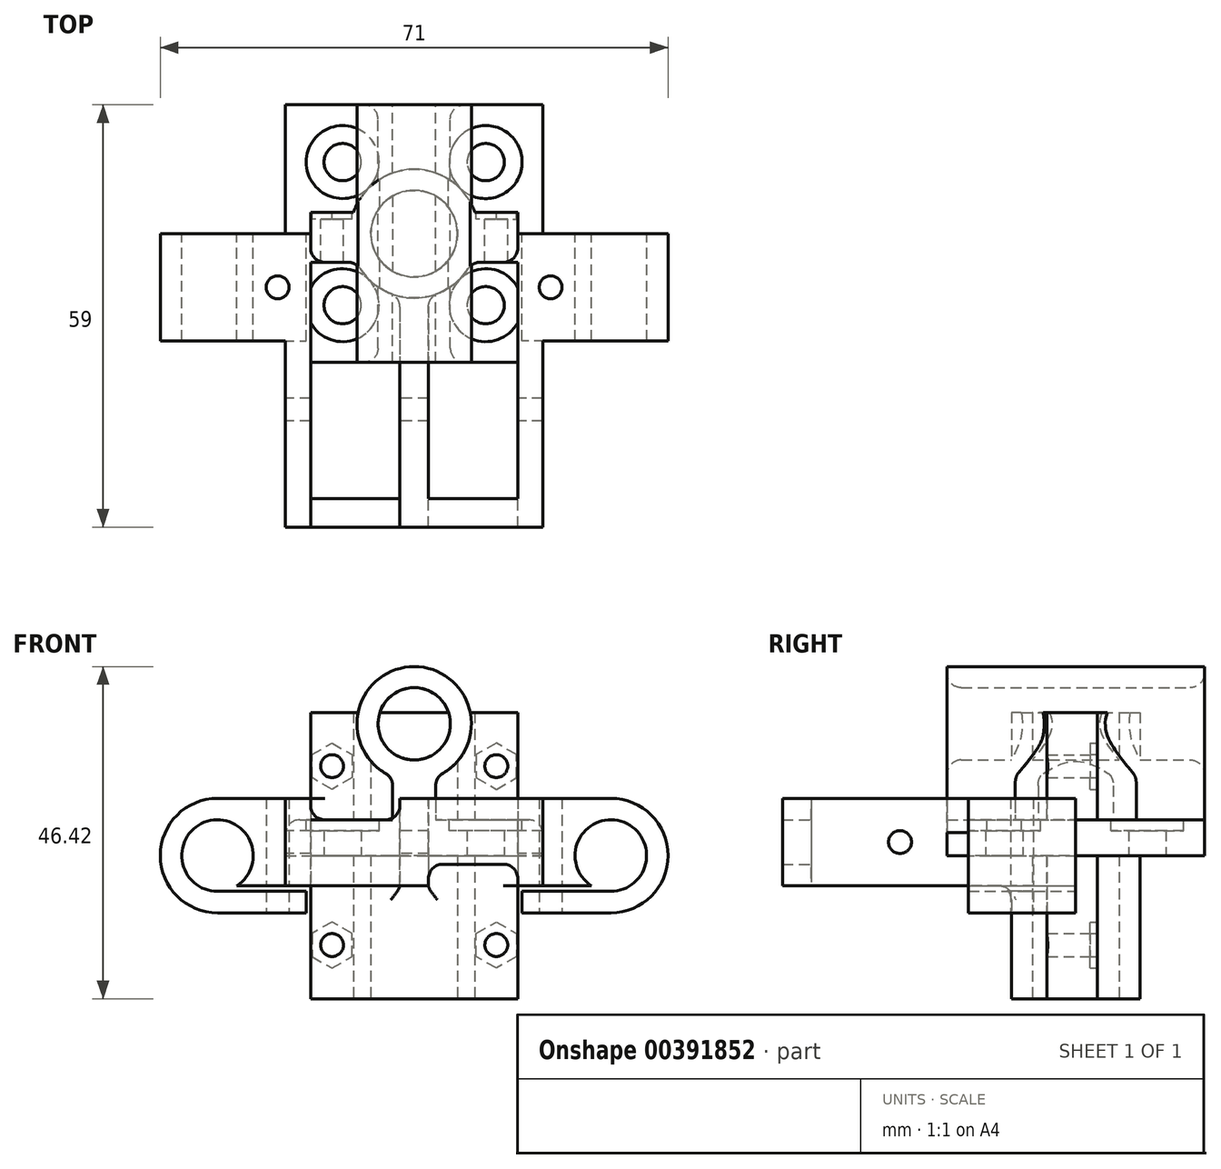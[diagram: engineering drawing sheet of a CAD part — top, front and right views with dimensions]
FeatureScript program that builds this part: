
annotation { "Feature Type Name" : "Feature", "Feature Type Description" : "" }
export const myFeature = defineFeature(function(context is Context, id is Id, definition is map)
    precondition{}
    {
        {
            var Q0;
            Q0=qCreatedBy(makeId("Top.planeOp"),FACE);
            var sketch = newSketch(context, id + "F0", { "sketchPlane" : qUnion([Q0])});
            skLineSegment(sketch, "E0.bottom", {"start": v(-18, 18) * mm, "end": v(18, 18) * mm});
            skLineSegment(sketch, "E0.top", {"start": v(-18, -18) * mm, "end": v(18, -18) * mm});
            skLineSegment(sketch, "E0.left", {"start": v(-18, 18) * mm, "end": v(-18, -18) * mm});
            skLineSegment(sketch, "E0.right", {"start": v(18, 18) * mm, "end": v(18, -18) * mm});
            skPoint(sketch, "E1", {"position": v(0, 18) * mm});
            skPoint(sketch, "E2", {"position": v(-18, 0) * mm});
            skCircle(sketch, "E3", {"center": v(-10, 10) * mm, "radius": 2.6 * mm});
            skCircle(sketch, "E4.MirrorC", {"center": v(-10, -10) * mm, "radius": 2.6 * mm});
            skCircle(sketch, "E5.MirrorC", {"center": v(10, 10) * mm, "radius": 2.6 * mm});
            skCircle(sketch, "E6.MirrorC", {"center": v(10, -10) * mm, "radius": 2.6 * mm});
            skSolve(sketch);
        }
        {
            var Q0;
            Q0=makeQuery(id+"F0.imprint","IMPRINT",FACE,{"disambiguationData":[TD([[makeQuery(id+"F0.imprint","IMPRINT",EDGE,{"derivedFrom":sQuery(id+"F0.wireOp",EDGE,"E0.bottom")}),-1.0]])]});
            extrude(context, id + "F1", {"entities" : qUnion([Q0]), "depth" : 5 * mm, "offsetDistance" : 25 * mm});
        }
        {
            var Q0;
            {var subQ0=sQuery(id+"F0.wireOp",EDGE,"E5.MirrorC");var subQ1=sQuery(id+"F0.wireOp",EDGE,"E0.top");var subQ7=sQuery(id+"F0.wireOp",EDGE,"E0.right");var subQ8=sQuery(id+"F0.wireOp",EDGE,"E0.bottom");var subQ9=sQuery(id+"F0.wireOp",EDGE,"E6.MirrorC");Q0=makeQuery(id+"F5.boolean.opBoolean","SPLIT",FACE,{"disambiguationData":[TD([makeQuery(id+"F1.opExtrude","SWEPT_FACE",FACE,{"disambiguationData":[OSD([subQ7])]})])],"derivedFrom":makeQuery(id+"F1.opExtrude","CAP_FACE",FACE,{"disambiguationData":[OSD([subQ8,subQ1,sQuery(id+"F0.wireOp",EDGE,"E0.left"),subQ7,sQuery(id+"F0.wireOp",EDGE,"E3"),sQuery(id+"F0.wireOp",EDGE,"E4.MirrorC"),subQ0,subQ9])],"isStart":false})});}
            var sketch = newSketch(context, id + "F2", { "sketchPlane" : qUnion([Q0])});
            skCircle(sketch, "E7", {"center": v(-10, 10) * mm, "radius": 5.1 * mm});
            skCircle(sketch, "E8.MirrorC", {"center": v(-10, -10) * mm, "radius": 5.1 * mm});
            skCircle(sketch, "E9.MirrorC", {"center": v(10, 10) * mm, "radius": 5.1 * mm});
            skCircle(sketch, "E10.MirrorC", {"center": v(10, -10) * mm, "radius": 5.1 * mm});
            skSolve(sketch);
        }
        {
            var Q0;
            Q0 = qSketchRegion(id + "F2", true);
            extrude(context, id + "F3", {"entities" : qUnion([Q0]), "operationType" : NewBodyOperationType.REMOVE, "oppositeDirection" : true, "depth" : 1.5 * mm, "offsetDistance" : 25 * mm});
        }
        {
            var Q0;
            Q0=qCreatedBy(makeId("Front.planeOp"),FACE);
            var sketch = newSketch(context, id + "F4", { "sketchPlane" : qUnion([Q0])});
            skLineSegment(sketch, "E11.top", {"start": v(-3, 5) * mm, "end": v(3, 5) * mm});
            skLineSegment(sketch, "E11.left", {"start": v(-3, 11) * mm, "end": v(-3, 5) * mm});
            skLineSegment(sketch, "E11.right", {"start": v(3, 11) * mm, "end": v(3, 5) * mm});
            skPoint(sketch, "E12", {"position": v(0, 11) * mm});
            skArc(sketch, "E13", {"start": v(3, 11) * mm, "mid": v(0, 26.42) * mm, "end": v(-3, 11) * mm});
            skCircle(sketch, "E14", {"center": v(0, 18.42) * mm, "radius": 5.05 * mm});
            skPoint(sketch, "E15", {"position": v(-3, 11) * mm});
            skSolve(sketch);
        }
        {
            var Q0;
            Q0=makeQuery(id+"F4.imprint","IMPRINT",FACE,{"disambiguationData":[TD([[makeQuery(id+"F4.imprint","IMPRINT",EDGE,{"derivedFrom":sQuery(id+"F4.wireOp",EDGE,"E11.top")}),1.0]])]});
            extrude(context, id + "F5", {"entities" : qUnion([Q0]), "operationType" : NewBodyOperationType.ADD, "depth" : 18 * mm, "offsetDistance" : 25 * mm, "hasSecondDirection" : true, "secondDirectionOppositeDirection" : true, "secondDirectionDepth" : 18 * mm});
        }
        {
            var Q0;
            Q0=makeQuery(id+"F5.opExtrude","CAP_EDGE",EDGE,{"disambiguationData":[OSD([sQuery(id+"F4.wireOp",EDGE,"E14")])],"isStart":false});
            var Q1;
            Q1=makeQuery(id+"F5.opExtrude","SWEPT_EDGE",EDGE,{"disambiguationData":[OSD([sQuery(id+"F4.wireOp",EDGE,"E11.top"),sQuery(id+"F4.wireOp",EDGE,"E11.left")])]});
            var Q2;
            Q2=makeQuery(id+"F5.opExtrude","SWEPT_EDGE",EDGE,{"disambiguationData":[OSD([sQuery(id+"F4.wireOp",EDGE,"E11.top"),sQuery(id+"F4.wireOp",EDGE,"E11.right")])]});
            var Q3;
            Q3=makeQuery(id+"F5.opExtrude","SWEPT_EDGE",EDGE,{"disambiguationData":[OSD([sQuery(id+"F4.wireOp",EDGE,"E11.right"),sQuery(id+"F4.wireOp",EDGE,"E13")])]});
            var Q4;
            Q4=makeQuery(id+"F5.opExtrude","SWEPT_EDGE",EDGE,{"disambiguationData":[OSD([sQuery(id+"F4.wireOp",EDGE,"E11.left"),sQuery(id+"F4.wireOp",EDGE,"E13")])]});
            var Q5;
            Q5=makeQuery(id+"F5.opExtrude","CAP_EDGE",EDGE,{"disambiguationData":[OSD([sQuery(id+"F4.wireOp",EDGE,"E14")])],"isStart":true});
            var Q6;
            Q6=makeQuery(id+"F1.opExtrude","CAP_EDGE",EDGE,{"disambiguationData":[OSD([sQuery(id+"F0.wireOp",EDGE,"E0.left")])],"isStart":false});
            var Q7;
            Q7=makeQuery(id+"F1.opExtrude","CAP_EDGE",EDGE,{"disambiguationData":[OSD([sQuery(id+"F0.wireOp",EDGE,"E0.right")])],"isStart":false});
            fillet(context, id + "F6", {"entities" : qUnion([Q0, Q1, Q2, Q3, Q4, Q5, Q6, Q7]), "radius" : 2 * mm, "tangentPropagation" : true, "allowEdgeOverflow" : false});
        }
        {
            var Q0;
            Q0=qCreatedBy(makeId("Top.planeOp"),FACE);
            var sketch = newSketch(context, id + "F7", { "sketchPlane" : qUnion([Q0])});
            skArc(sketch, "E16", {"start": v(6.05, 0) * mm, "mid": v(0, 6.05) * mm, "end": v(-6.05, 0) * mm});
            skArc(sketch, "E17", {"start": v(8.49, 3) * mm, "mid": v(0, 9) * mm, "end": v(-8.49, 3) * mm});
            skLineSegment(sketch, "E18", {"start": v(-9, 0) * mm, "end": v(-14.49, 0) * mm});
            skLineSegment(sketch, "E19", {"start": v(-14.49, 0) * mm, "end": v(-14.49, 3) * mm});
            skLineSegment(sketch, "E20", {"start": v(-14.49, 3) * mm, "end": v(-8.49, 3) * mm});
            skLineSegment(sketch, "E21", {"start": v(-6.05, 0) * mm, "end": v(-9, 0) * mm});
            skLineSegment(sketch, "E22.MirrorCS", {"start": v(14.49, 3) * mm, "end": v(8.49, 3) * mm});
            skLineSegment(sketch, "E23.MirrorCS", {"start": v(14.49, 0) * mm, "end": v(14.49, 3) * mm});
            skLineSegment(sketch, "E24.MirrorCS", {"start": v(9, 0) * mm, "end": v(14.49, 0) * mm});
            skLineSegment(sketch, "E25.MirrorCS", {"start": v(6.05, 0) * mm, "end": v(9, 0) * mm});
            skPoint(sketch, "E26.orphan", {"position": v(9, 0) * mm});
            skSolve(sketch);
        }
        {
            var Q0;
            Q0=makeQuery(id+"F7.imprint","IMPRINT",FACE,{"disambiguationData":[TD([[makeQuery(id+"F7.imprint","IMPRINT",EDGE,{"derivedFrom":sQuery(id+"F7.wireOp",EDGE,"E16")}),-1.0]])]});
            extrude(context, id + "F8", {"entities" : qUnion([Q0]), "depth" : 20 * mm, "offsetDistance" : 25 * mm, "hasSecondDirection" : true, "secondDirectionOppositeDirection" : true, "secondDirectionDepth" : 20 * mm});
        }
        {
            var Q0;
            Q0=makeQuery(id+"F8.opExtrude","SWEPT_FACE",FACE,{"disambiguationData":[OSD([sQuery(id+"F7.wireOp",EDGE,"E20")])]});
            var sketch = newSketch(context, id + "F9", { "sketchPlane" : qUnion([Q0])});
            skCircle(sketch, "E27", {"center": v(11.49, -12.5) * mm, "radius": 1.6 * mm});
            skCircle(sketch, "E28.MirrorC", {"center": v(11.49, 12.5) * mm, "radius": 1.6 * mm});
            skCircle(sketch, "E29.MirrorC", {"center": v(-11.49, -12.5) * mm, "radius": 1.6 * mm});
            skCircle(sketch, "E30.MirrorC", {"center": v(-11.49, 12.5) * mm, "radius": 1.6 * mm});
            skSolve(sketch);
        }
        {
            var Q0;
            Q0=makeQuery(id+"F8.opExtrude","SWEPT_FACE",FACE,{"disambiguationData":[OSD([sQuery(id+"F7.wireOp",EDGE,"E20")])]});
            var sketch = newSketch(context, id + "F10", { "sketchPlane" : qUnion([Q0])});
            skCircle(sketch, "E31.cCircle", {"center": v(11.49, -12.5) * mm, "radius": 2.8 * mm, "construction": true});
            skLineSegment(sketch, "E31.0", {"start": v(8.69, -10.88) * mm, "end": v(11.49, -9.27) * mm});
            skLineSegment(sketch, "E31.1", {"start": v(11.49, -9.27) * mm, "end": v(14.29, -10.88) * mm});
            skLineSegment(sketch, "E31.2", {"start": v(14.29, -10.88) * mm, "end": v(14.29, -14.12) * mm});
            skLineSegment(sketch, "E31.3", {"start": v(14.29, -14.12) * mm, "end": v(11.49, -15.73) * mm});
            skLineSegment(sketch, "E31.4", {"start": v(11.49, -15.73) * mm, "end": v(8.69, -14.12) * mm});
            skLineSegment(sketch, "E31.5", {"start": v(8.69, -14.12) * mm, "end": v(8.69, -10.88) * mm});
            skPoint(sketch, "E31.0.midPoint", {"position": v(10.09, -10.08) * mm});
            skPoint(sketch, "E32.MirrorP", {"position": v(10.09, 10.08) * mm});
            skCircle(sketch, "E33.MirrorC", {"center": v(11.49, 12.5) * mm, "radius": 2.8 * mm, "construction": true});
            skLineSegment(sketch, "E34.MirrorCS", {"start": v(8.69, 10.88) * mm, "end": v(11.49, 9.27) * mm});
            skLineSegment(sketch, "E35.MirrorCS", {"start": v(11.49, 9.27) * mm, "end": v(14.29, 10.88) * mm});
            skLineSegment(sketch, "E36.MirrorCS", {"start": v(14.29, 10.88) * mm, "end": v(14.29, 14.12) * mm});
            skLineSegment(sketch, "E37.MirrorCS", {"start": v(14.29, 14.12) * mm, "end": v(11.49, 15.73) * mm});
            skLineSegment(sketch, "E38.MirrorCS", {"start": v(11.49, 15.73) * mm, "end": v(8.69, 14.12) * mm});
            skLineSegment(sketch, "E39.MirrorCS", {"start": v(8.69, 14.12) * mm, "end": v(8.69, 10.88) * mm});
            skLineSegment(sketch, "E40.MirrorCS", {"start": v(-11.49, 9.27) * mm, "end": v(-14.29, 10.88) * mm});
            skLineSegment(sketch, "E41.MirrorCS", {"start": v(-8.69, 10.88) * mm, "end": v(-11.49, 9.27) * mm});
            skCircle(sketch, "E42.MirrorC", {"center": v(-11.49, 12.5) * mm, "radius": 2.8 * mm, "construction": true});
            skLineSegment(sketch, "E43.MirrorCS", {"start": v(-8.69, -14.12) * mm, "end": v(-8.69, -10.88) * mm});
            skLineSegment(sketch, "E44.MirrorCS", {"start": v(-11.49, -15.73) * mm, "end": v(-8.69, -14.12) * mm});
            skLineSegment(sketch, "E45.MirrorCS", {"start": v(-14.29, -14.12) * mm, "end": v(-11.49, -15.73) * mm});
            skLineSegment(sketch, "E46.MirrorCS", {"start": v(-14.29, -10.88) * mm, "end": v(-14.29, -14.12) * mm});
            skLineSegment(sketch, "E47.MirrorCS", {"start": v(-11.49, -9.27) * mm, "end": v(-14.29, -10.88) * mm});
            skLineSegment(sketch, "E48.MirrorCS", {"start": v(-8.69, -10.88) * mm, "end": v(-11.49, -9.27) * mm});
            skCircle(sketch, "E49.MirrorC", {"center": v(-11.49, -12.5) * mm, "radius": 2.8 * mm, "construction": true});
            skLineSegment(sketch, "E50.MirrorCS", {"start": v(-8.69, 14.12) * mm, "end": v(-8.69, 10.88) * mm});
            skPoint(sketch, "E51.MirrorP", {"position": v(-10.09, 10.08) * mm});
            skLineSegment(sketch, "E52.MirrorCS", {"start": v(-11.49, 15.73) * mm, "end": v(-8.69, 14.12) * mm});
            skPoint(sketch, "E53.MirrorP", {"position": v(-10.09, -10.08) * mm});
            skLineSegment(sketch, "E54.MirrorCS", {"start": v(-14.29, 14.12) * mm, "end": v(-11.49, 15.73) * mm});
            skLineSegment(sketch, "E55.MirrorCS", {"start": v(-14.29, 10.88) * mm, "end": v(-14.29, 14.12) * mm});
            skSolve(sketch);
        }
        {
            var Q0;
            Q0 = qSketchRegion(id + "F10", true);
            extrude(context, id + "F11", {"entities" : qUnion([Q0]), "operationType" : NewBodyOperationType.REMOVE, "oppositeDirection" : true, "depth" : 1 * mm, "offsetDistance" : 25 * mm});
        }
        {
            var Q0;
            Q0=qCreatedBy(makeId("Top.planeOp"),FACE);
            var sketch = newSketch(context, id + "F12", { "sketchPlane" : qUnion([Q0])});
            skPoint(sketch, "E56.0", {"position": v(6.05, 0) * mm});
            skPoint(sketch, "E57.0", {"position": v(-6.05, 0) * mm});
            skArc(sketch, "E58", {"start": v(-6.05, 0) * mm, "mid": v(0, -6.05) * mm, "end": v(6.05, 0) * mm});
            skLineSegment(sketch, "E59", {"start": v(6.05, 0) * mm, "end": v(14.49, 0) * mm});
            skLineSegment(sketch, "E60", {"start": v(14.49, 0) * mm, "end": v(14.49, -4) * mm});
            skLineSegment(sketch, "E61", {"start": v(14.49, -4) * mm, "end": v(8.06, -4) * mm});
            skLineSegment(sketch, "E62.MirrorCS", {"start": v(-6.05, 0) * mm, "end": v(-14.49, 0) * mm});
            skLineSegment(sketch, "E63.MirrorCS", {"start": v(-14.49, 0) * mm, "end": v(-14.49, -4) * mm});
            skLineSegment(sketch, "E64.MirrorCS", {"start": v(-14.49, -4) * mm, "end": v(-8.06, -4) * mm});
            skArc(sketch, "E65", {"start": v(-8.06, -4) * mm, "mid": v(0, -9) * mm, "end": v(8.06, -4) * mm});
            skPoint(sketch, "E66.orphan", {"position": v(4.54, -4) * mm});
            skPoint(sketch, "E67.orphan", {"position": v(-4.54, -4) * mm});
            skSolve(sketch);
        }
        {
            var Q0;
            Q0=makeQuery(id+"F12.imprint","IMPRINT",FACE,{"disambiguationData":[TD([[makeQuery(id+"F12.imprint","IMPRINT",EDGE,{"derivedFrom":sQuery(id+"F12.wireOp",EDGE,"E58")}),-1.0]])]});
            extrude(context, id + "F13", {"entities" : qUnion([Q0]), "depth" : 20 * mm, "offsetDistance" : 25 * mm, "hasSecondDirection" : true, "secondDirectionOppositeDirection" : true, "secondDirectionDepth" : 20 * mm});
        }
        {
            var Q0;
            Q0 = qSketchRegion(id + "F9", true);
            extrude(context, id + "F14", {"entities" : qUnion([Q0]), "operationType" : NewBodyOperationType.REMOVE, "oppositeDirection" : true, "depth" : 10 * mm, "offsetDistance" : 25 * mm});
        }
        {
            var Q0;
            Q0=qCreatedBy(makeId("Front.planeOp"),FACE);
            var sketch = newSketch(context, id + "F15", { "sketchPlane" : qUnion([Q0])});
            skArc(sketch, "E68", {"start": v(27.5, -5) * mm, "mid": v(28.91, 4.8) * mm, "end": v(24.79, -4.2) * mm});
            skLineSegment(sketch, "E69", {"start": v(27.5, 8) * mm, "end": v(14.49, 8) * mm});
            skLineSegment(sketch, "E70", {"start": v(14.49, 8) * mm, "end": v(14.49, -4.2) * mm});
            skLineSegment(sketch, "E71", {"start": v(14.49, -4.2) * mm, "end": v(24.79, -4.2) * mm});
            skLineSegment(sketch, "E72", {"start": v(27.5, -5) * mm, "end": v(15.09, -5) * mm});
            skLineSegment(sketch, "E73", {"start": v(15.09, -5) * mm, "end": v(15.09, -8) * mm});
            skLineSegment(sketch, "E74", {"start": v(15.09, -8) * mm, "end": v(27.5, -8) * mm});
            skLineSegment(sketch, "E75.bottom", {"start": v(20.58, 25.4) * mm, "end": v(17.38, 25.4) * mm, "construction": true});
            skLineSegment(sketch, "E75.top", {"start": v(20.58, -14.77) * mm, "end": v(17.38, -14.77) * mm, "construction": true});
            skLineSegment(sketch, "E75.left", {"start": v(20.58, 25.4) * mm, "end": v(20.58, -14.77) * mm, "construction": true});
            skLineSegment(sketch, "E75.right", {"start": v(17.38, 25.4) * mm, "end": v(17.38, -14.77) * mm, "construction": true});
            skArc(sketch, "E76.trimOffspring", {"start": v(27.5, -8) * mm, "mid": v(31.4, 6.99) * mm, "end": v(20.7, -4.2) * mm});
            skLineSegment(sketch, "E77.MirrorCS", {"start": v(-14.49, 8) * mm, "end": v(-14.49, -4.2) * mm});
            skArc(sketch, "E78.MirrorCS", {"start": v(-27.5, -5) * mm, "mid": v(-28.91, 4.8) * mm, "end": v(-24.79, -4.2) * mm});
            skLineSegment(sketch, "E79.MirrorCS", {"start": v(-27.5, 8) * mm, "end": v(-14.49, 8) * mm});
            skLineSegment(sketch, "E80.MirrorCS", {"start": v(-15.09, -8) * mm, "end": v(-27.5, -8) * mm});
            skLineSegment(sketch, "E81.MirrorCS", {"start": v(-14.49, -4.2) * mm, "end": v(-24.79, -4.2) * mm});
            skLineSegment(sketch, "E82.MirrorCS", {"start": v(-15.09, -5) * mm, "end": v(-15.09, -8) * mm});
            skArc(sketch, "E83.MirrorCS", {"start": v(-27.5, -8) * mm, "mid": v(-31.4, 6.99) * mm, "end": v(-20.7, -4.2) * mm});
            skLineSegment(sketch, "E84.MirrorCS", {"start": v(-27.5, -5) * mm, "end": v(-15.09, -5) * mm});
            skSolve(sketch);
        }
        {
            var Q0;
            Q0 = qSketchRegion(id + "F15", true);
            extrude(context, id + "F16", {"entities" : qUnion([Q0]), "operationType" : NewBodyOperationType.ADD, "depth" : 15 * mm, "offsetDistance" : 25 * mm});
        }
        {
            var Q0;
            Q0=makeQuery(id+"F16.opExtrude","CAP_FACE",FACE,{"disambiguationData":[OSD([sQuery(id+"F15.wireOp",EDGE,"E68"),sQuery(id+"F15.wireOp",EDGE,"E69"),sQuery(id+"F15.wireOp",EDGE,"E70"),sQuery(id+"F15.wireOp",EDGE,"E71"),sQuery(id+"F15.wireOp",EDGE,"E72"),sQuery(id+"F15.wireOp",EDGE,"E73"),sQuery(id+"F15.wireOp",EDGE,"E74"),sQuery(id+"F15.wireOp",EDGE,"E76.trimOffspring")])],"isStart":false});
            var sketch = newSketch(context, id + "F17", { "sketchPlane" : qUnion([Q0])});
            skLineSegment(sketch, "E85.bottom", {"start": v(14.49, 8) * mm, "end": v(17.99, 8) * mm});
            skLineSegment(sketch, "E85.top", {"start": v(14.49, -4.2) * mm, "end": v(17.99, -4.2) * mm});
            skLineSegment(sketch, "E85.left", {"start": v(14.49, 8) * mm, "end": v(14.49, -4.2) * mm});
            skLineSegment(sketch, "E85.right", {"start": v(17.99, 8) * mm, "end": v(17.99, -4.2) * mm});
            skLineSegment(sketch, "E86.MirrorCS", {"start": v(-17.99, 8) * mm, "end": v(-17.99, -4.2) * mm});
            skLineSegment(sketch, "E87.MirrorCS", {"start": v(-14.49, 8) * mm, "end": v(-14.49, -4.2) * mm});
            skLineSegment(sketch, "E88.MirrorCS", {"start": v(-14.49, -4.2) * mm, "end": v(-17.99, -4.2) * mm});
            skLineSegment(sketch, "E89.MirrorCS", {"start": v(-14.49, 8) * mm, "end": v(-17.99, 8) * mm});
            skSolve(sketch);
        }
        {
            var Q0;
            Q0 = qSketchRegion(id + "F17", true);
            extrude(context, id + "F18", {"entities" : qUnion([Q0]), "operationType" : NewBodyOperationType.ADD, "depth" : 22 * mm, "offsetDistance" : 25 * mm});
        }
        {
            var Q0;
            Q0=makeQuery(id+"F18.opExtrude","CAP_FACE",FACE,{"disambiguationData":[OSD([sQuery(id+"F17.wireOp",EDGE,"E85.bottom"),sQuery(id+"F17.wireOp",EDGE,"E85.top"),sQuery(id+"F17.wireOp",EDGE,"E85.left"),sQuery(id+"F17.wireOp",EDGE,"E85.right")])],"isStart":false});
            var sketch = newSketch(context, id + "F19", { "sketchPlane" : qUnion([Q0])});
            skLineSegment(sketch, "E90.bottom", {"start": v(17.99, 8) * mm, "end": v(-2, 8) * mm});
            skLineSegment(sketch, "E90.top", {"start": v(17.99, -4.2) * mm, "end": v(14.49, -4.2) * mm});
            skLineSegment(sketch, "E90.left", {"start": v(17.99, 8) * mm, "end": v(17.99, -4.2) * mm});
            skLineSegment(sketch, "E90.right", {"start": v(-17.99, 8) * mm, "end": v(-17.99, -4.2) * mm});
            skLineSegment(sketch, "E91", {"start": v(2, 8) * mm, "end": v(2, -4.2) * mm});
            skLineSegment(sketch, "E92", {"start": v(-2, 8) * mm, "end": v(-2, -4.2) * mm});
            skLineSegment(sketch, "E93", {"start": v(14.49, -1.2) * mm, "end": v(2, -1.2) * mm});
            skPoint(sketch, "E93.endSnap0", {"position": v(-2, 5) * mm});
            skLineSegment(sketch, "E94", {"start": v(14.49, 1.9) * mm, "end": v(14.49, -4.2) * mm});
            skLineSegment(sketch, "E95", {"start": v(-14.49, 1.9) * mm, "end": v(-14.49, 8) * mm});
            skLineSegment(sketch, "E96.trimOffspring", {"start": v(2, -4.2) * mm, "end": v(-17.99, -4.2) * mm});
            skLineSegment(sketch, "E97.trimOffspring", {"start": v(-14.49, 8) * mm, "end": v(-17.99, 8) * mm});
            skLineSegment(sketch, "E98.trimOffspring", {"start": v(-2, 5) * mm, "end": v(-14.49, 5) * mm});
            skSolve(sketch);
        }
        {
            var Q0;
            Q0 = qSketchRegion(id + "F19", true);
            extrude(context, id + "F20", {"entities" : qUnion([Q0]), "operationType" : NewBodyOperationType.ADD, "depth" : 4 * mm, "offsetDistance" : 25 * mm});
        }
        {
            var Q0;
            {var subQ1=sQuery(id+"F19.wireOp",EDGE,"E90.bottom");var subQ5=sQuery(id+"F19.wireOp",EDGE,"E91");var subQ8=makeQuery(id+"F19.imprint","INTERSECT",VERTEX,{"derivedFrom":[subQ1,subQ5]});Q0=makeQuery(id+"F19.imprint","IMPRINT",FACE,{"disambiguationData":[TD([[makeQuery(id+"F19.imprint","IMPRINT",EDGE,{"disambiguationData":[TD([[subQ8,-1.0]])],"derivedFrom":subQ1}),1.0]])]});}
            extrude(context, id + "F21", {"entities" : qUnion([Q0]), "operationType" : NewBodyOperationType.ADD, "oppositeDirection" : true, "depth" : 30 * mm, "offsetDistance" : 25 * mm});
        }
        {
            var Q0;
            Q0=qCreatedBy(makeId("Right.planeOp"),FACE);
            var sketch = newSketch(context, id + "F22", { "sketchPlane" : qUnion([Q0])});
            skCircle(sketch, "E99", {"center": v(-24.57, 1.9) * mm, "radius": 1.6 * mm});
            skCircle(sketch, "E100", {"center": v(-24.57, 1.9) * mm, "radius": 11 * mm, "construction": true});
            skSolve(sketch);
        }
        {
            var Q0;
            Q0 = qSketchRegion(id + "F22", true);
            extrude(context, id + "F23", {"entities" : qUnion([Q0]), "operationType" : NewBodyOperationType.REMOVE, "depth" : 25 * mm, "offsetDistance" : 25 * mm, "hasSecondDirection" : true, "secondDirectionOppositeDirection" : true, "secondDirectionDepth" : 25 * mm});
        }
        {
            var Q0;
            Q0=makeQuery(id+"F21.boolean.opBoolean","INTERSECT",EDGE,{"derivedFrom":[makeQuery(id+"F13.opExtrude","SWEPT_FACE",FACE,{"disambiguationData":[OSD([sQuery(id+"F12.wireOp",EDGE,"E65")])]}),makeQuery(id+"F21.opExtrude","SWEPT_FACE",FACE,{"disambiguationData":[OSD([sQuery(id+"F19.wireOp",EDGE,"E90.bottom")])]})]});
            var Q1;
            Q1=makeQuery(id+"F21.boolean.opBoolean","INTERSECT",EDGE,{"derivedFrom":[makeQuery(id+"F13.opExtrude","SWEPT_FACE",FACE,{"disambiguationData":[OSD([sQuery(id+"F12.wireOp",EDGE,"E65")])]}),makeQuery(id+"F21.opExtrude","SWEPT_FACE",FACE,{"disambiguationData":[OSD([sQuery(id+"F19.wireOp",EDGE,"E92")])]})]});
            var Q2;
            Q2=makeQuery(id+"F21.boolean.opBoolean","INTERSECT",EDGE,{"derivedFrom":[makeQuery(id+"F13.opExtrude","SWEPT_FACE",FACE,{"disambiguationData":[OSD([sQuery(id+"F12.wireOp",EDGE,"E65")])]}),makeQuery(id+"F21.opExtrude","SWEPT_FACE",FACE,{"disambiguationData":[OSD([sQuery(id+"F19.wireOp",EDGE,"E91")])]})]});
            var Q3;
            Q3=makeQuery(id+"F21.boolean.opBoolean","INTERSECT",EDGE,{"derivedFrom":[makeQuery(id+"F13.opExtrude","SWEPT_FACE",FACE,{"disambiguationData":[OSD([sQuery(id+"F12.wireOp",EDGE,"E65")])]}),makeQuery(id+"F21.opExtrude","SWEPT_FACE",FACE,{"disambiguationData":[OSD([sQuery(id+"F19.wireOp",EDGE,"E96.trimOffspring")])]})]});
            var Q4;
            {var subQ0=sQuery(id+"F12.wireOp",EDGE,"E61");Q4=makeQuery(id+"F16.boolean.opBoolean","SPLIT",EDGE,{"disambiguationData":[topologyDisambiguationEdgeConnected([makeQuery(id+"F13.opExtrude","SWEPT_FACE",FACE,{"disambiguationData":[OSD([subQ0])]}),makeQuery(id+"F16.opExtrude","SWEPT_FACE",FACE,{"disambiguationData":[OSD([sQuery(id+"F15.wireOp",EDGE,"E70")])]})])],"derivedFrom":makeQuery(id+"F13.opExtrude","SWEPT_EDGE",EDGE,{"disambiguationData":[OSD([sQuery(id+"F12.wireOp",EDGE,"E60"),subQ0])]})});}
            var Q5;
            Q5=makeQuery(id+"F13.opExtrude","SWEPT_EDGE",EDGE,{"disambiguationData":[OSD([sQuery(id+"F12.wireOp",EDGE,"E61"),sQuery(id+"F12.wireOp",EDGE,"E65")])]});
            var Q6;
            Q6=makeQuery(id+"F13.opExtrude","SWEPT_EDGE",EDGE,{"disambiguationData":[OSD([sQuery(id+"F12.wireOp",EDGE,"E64.MirrorCS"),sQuery(id+"F12.wireOp",EDGE,"E65")])]});
            var Q7;
            {var subQ0=sQuery(id+"F12.wireOp",EDGE,"E64.MirrorCS");Q7=makeQuery(id+"F16.boolean.opBoolean","SPLIT",EDGE,{"disambiguationData":[topologyDisambiguationEdgeConnected([makeQuery(id+"F13.opExtrude","SWEPT_FACE",FACE,{"disambiguationData":[OSD([subQ0])]}),makeQuery(id+"F16.opExtrude","SWEPT_FACE",FACE,{"disambiguationData":[OSD([sQuery(id+"F15.wireOp",EDGE,"E77.MirrorCS")])]})])],"derivedFrom":makeQuery(id+"F13.opExtrude","SWEPT_EDGE",EDGE,{"disambiguationData":[OSD([sQuery(id+"F12.wireOp",EDGE,"E63.MirrorCS"),subQ0])]})});}
            var Q8;
            Q8=makeQuery(id+"F21.opExtrude","CAP_EDGE",EDGE,{"disambiguationData":[OSD([sQuery(id+"F19.wireOp",EDGE,"E91")])],"isStart":true});
            var Q9;
            Q9=makeQuery(id+"F18.opExtrude","CAP_EDGE",EDGE,{"disambiguationData":[OSD([sQuery(id+"F17.wireOp",EDGE,"E85.left")])],"isStart":false});
            var Q10;
            Q10=makeQuery(id+"F21.opExtrude","CAP_EDGE",EDGE,{"disambiguationData":[OSD([sQuery(id+"F19.wireOp",EDGE,"E92")])],"isStart":true});
            var Q11;
            Q11=makeQuery(id+"F18.opExtrude","CAP_EDGE",EDGE,{"disambiguationData":[OSD([sQuery(id+"F17.wireOp",EDGE,"E87.MirrorCS")])],"isStart":false});
            var Q12;
            Q12=makeQuery(id+"F20.opExtrude","SWEPT_EDGE",EDGE,{"disambiguationData":[OSD([sQuery(id+"F19.wireOp",EDGE,"E92"),sQuery(id+"F19.wireOp",EDGE,"E98.trimOffspring")])]});
            var Q13;
            Q13=makeQuery(id+"F20.opExtrude","SWEPT_EDGE",EDGE,{"disambiguationData":[OSD([sQuery(id+"F19.wireOp",EDGE,"E91"),sQuery(id+"F19.wireOp",EDGE,"E93")])]});
            var Q14;
            Q14=makeQuery(id+"F20.opExtrude","SWEPT_EDGE",EDGE,{"disambiguationData":[OSD([sQuery(id+"F17.wireOp",EDGE,"E85.left"),sQuery(id+"F19.wireOp",EDGE,"E93"),sQuery(id+"F19.wireOp",EDGE,"E94")])]});
            var Q15;
            Q15=makeQuery(id+"F20.opExtrude","SWEPT_EDGE",EDGE,{"disambiguationData":[OSD([sQuery(id+"F19.wireOp",EDGE,"E95"),sQuery(id+"F19.wireOp",EDGE,"E98.trimOffspring")])]});
            var Q16;
            Q16=makeQuery(id+"F18.opExtrude","CAP_EDGE",EDGE,{"disambiguationData":[OSD([sQuery(id+"F17.wireOp",EDGE,"E85.right")])],"isStart":true});
            var Q17;
            Q17=makeQuery(id+"F18.opExtrude","CAP_EDGE",EDGE,{"disambiguationData":[OSD([sQuery(id+"F17.wireOp",EDGE,"E86.MirrorCS")])],"isStart":true});
            fillet(context, id + "F24", {"entities" : qUnion([Q0, Q1, Q2, Q3, Q4, Q5, Q6, Q7, Q8, Q9, Q10, Q11, Q12, Q13, Q14, Q15, Q16, Q17]), "radius" : 2 * mm, "tangentPropagation" : true, "allowEdgeOverflow" : false});
        }
        {
            var Q0;
            Q0=makeQuery(id+"F16.opExtrude","SWEPT_FACE",FACE,{"disambiguationData":[OSD([sQuery(id+"F15.wireOp",EDGE,"E80.MirrorCS")])]});
            var sketch = newSketch(context, id + "F25", { "sketchPlane" : qUnion([Q0])});
            skCircle(sketch, "E101", {"center": v(-19.09, 7.5) * mm, "radius": 1.6 * mm});
            skCircle(sketch, "E102.MirrorC", {"center": v(19.09, 7.5) * mm, "radius": 1.6 * mm});
            skSolve(sketch);
        }
        {
            var Q0;
            Q0 = qSketchRegion(id + "F25", true);
            extrude(context, id + "F26", {"entities" : qUnion([Q0]), "operationType" : NewBodyOperationType.REMOVE, "oppositeDirection" : true, "depth" : 17.1 * mm, "offsetDistance" : 25 * mm});
        }
    });
